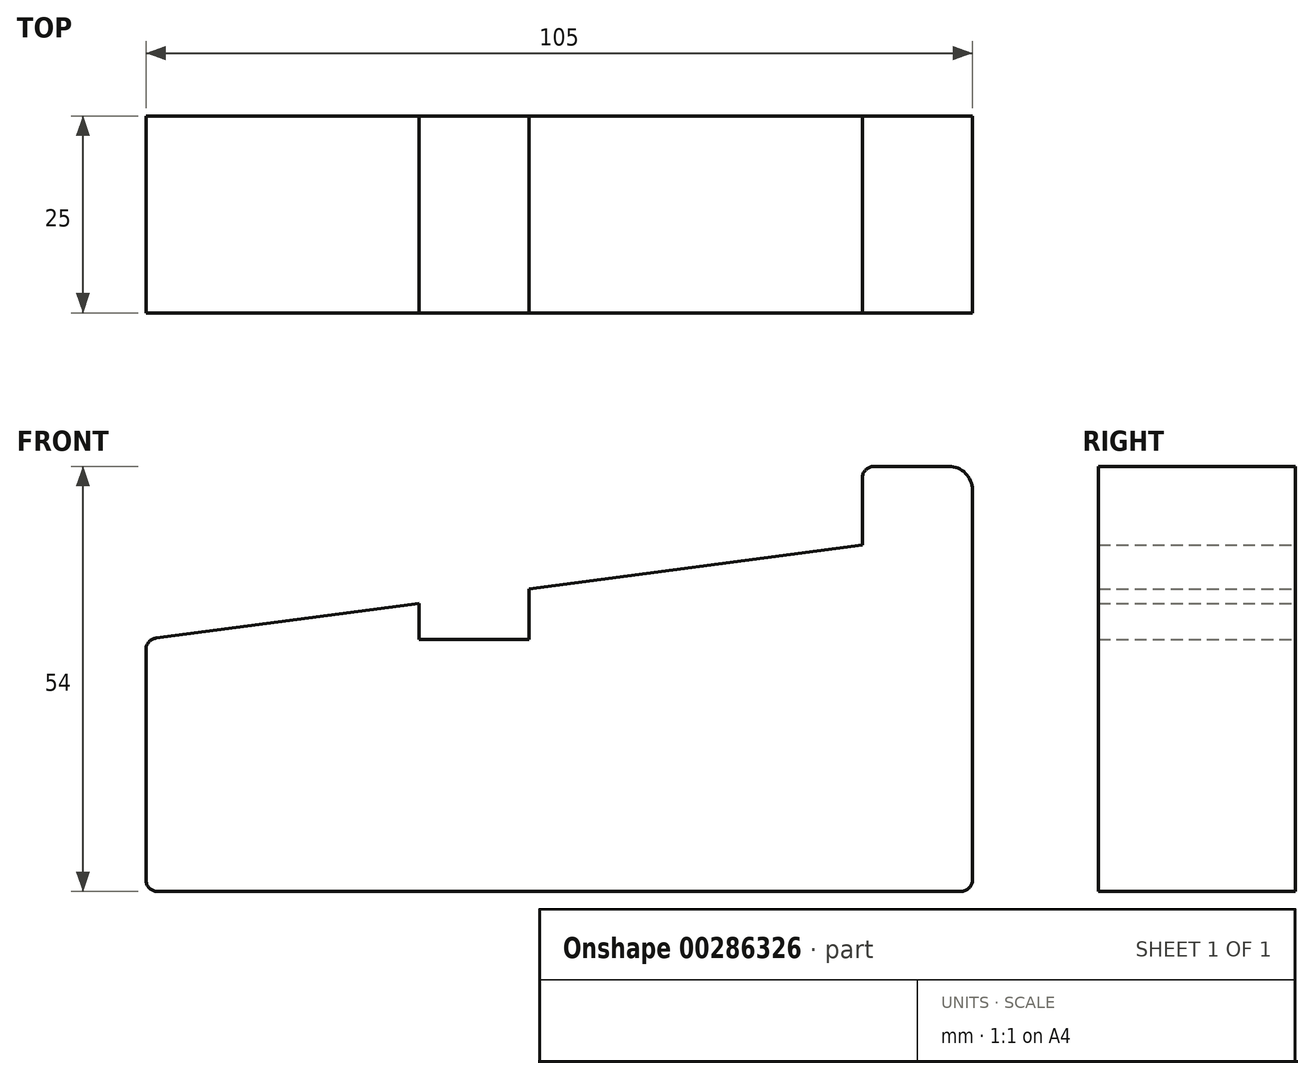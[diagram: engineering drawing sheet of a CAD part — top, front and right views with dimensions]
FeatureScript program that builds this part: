
annotation { "Feature Type Name" : "Feature", "Feature Type Description" : "" }
export const myFeature = defineFeature(function(context is Context, id is Id, definition is map)
    precondition{}
    {
        {
            var Q0;
            Q0=qCreatedBy(makeId("Front.planeOp"),FACE);
            var sketch = newSketch(context, id + "F0", { "sketchPlane" : qUnion([Q0])});
            skLineSegment(sketch, "E0", {"start": v(34.35, -44) * mm, "end": v(-67.65, -44) * mm});
            skLineSegment(sketch, "E1", {"start": v(35.85, -42.5) * mm, "end": v(35.85, 7) * mm});
            skLineSegment(sketch, "E2", {"start": v(32.85, 10) * mm, "end": v(23.35, 10) * mm});
            skPoint(sketch, "E3.visualSharp", {"position": v(35.85, 10) * mm});
            skArc(sketch, "E3.filletArc", {"start": v(35.85, 7) * mm, "mid": v(34.97, 9.12) * mm, "end": v(32.85, 10) * mm});
            skLineSegment(sketch, "E4", {"start": v(21.85, 8.5) * mm, "end": v(21.85, 0) * mm});
            skPoint(sketch, "E5.visualSharp", {"position": v(21.85, 10) * mm});
            skArc(sketch, "E5.filletArc", {"start": v(23.35, 10) * mm, "mid": v(22.29, 9.56) * mm, "end": v(21.85, 8.5) * mm});
            skLineSegment(sketch, "E6", {"start": v(-69.15, -42.5) * mm, "end": v(-69.15, -13.32) * mm});
            skLineSegment(sketch, "E7", {"start": v(-67.85, -11.83) * mm, "end": v(-34.45, -7.42) * mm});
            skPoint(sketch, "E8.visualSharp", {"position": v(-69.15, -12) * mm});
            skArc(sketch, "E8.filletArc", {"start": v(-67.85, -11.83) * mm, "mid": v(-68.78, -12.33) * mm, "end": v(-69.15, -13.32) * mm});
            skPoint(sketch, "E9.visualSharp", {"position": v(-69.15, -44) * mm});
            skArc(sketch, "E9.filletArc", {"start": v(-69.15, -42.5) * mm, "mid": v(-68.71, -43.56) * mm, "end": v(-67.65, -44) * mm});
            skPoint(sketch, "E10.visualSharp", {"position": v(35.85, -44) * mm});
            skArc(sketch, "E10.filletArc", {"start": v(34.35, -44) * mm, "mid": v(35.41, -43.56) * mm, "end": v(35.85, -42.5) * mm});
            skLineSegment(sketch, "E11", {"start": v(-69.15, -12) * mm, "end": v(-34.45, -7.42) * mm});
            skLineSegment(sketch, "E12", {"start": v(-34.45, -7.42) * mm, "end": v(-34.45, -12) * mm});
            skLineSegment(sketch, "E13", {"start": v(-34.45, -44) * mm, "end": v(-34.45, -12) * mm});
            skLineSegment(sketch, "E14", {"start": v(-34.45, -12) * mm, "end": v(-20.45, -12) * mm});
            skLineSegment(sketch, "E15", {"start": v(-20.45, -12) * mm, "end": v(-20.45, -5.58) * mm});
            skLineSegment(sketch, "E16.trimOffspring", {"start": v(-20.45, -5.58) * mm, "end": v(21.85, 0) * mm});
            skSolve(sketch);
        }
        {
            var Q0;
            Q0=makeQuery(id+"F0.imprint","IMPRINT",FACE,{"disambiguationData":[TD([[makeQuery(id+"F0.imprint","IMPRINT",EDGE,{"derivedFrom":sQuery(id+"F0.wireOp",EDGE,"E6")}),-1.0]])]});
            var Q1;
            Q1=makeQuery(id+"F0.imprint","IMPRINT",FACE,{"disambiguationData":[TD([[makeQuery(id+"F0.imprint","IMPRINT",EDGE,{"derivedFrom":sQuery(id+"F0.wireOp",EDGE,"E1")}),1.0]])]});
            extrude(context, id + "F1", {"entities" : qUnion([Q0, Q1]), "depth" : 25 * mm});
        }
    });
